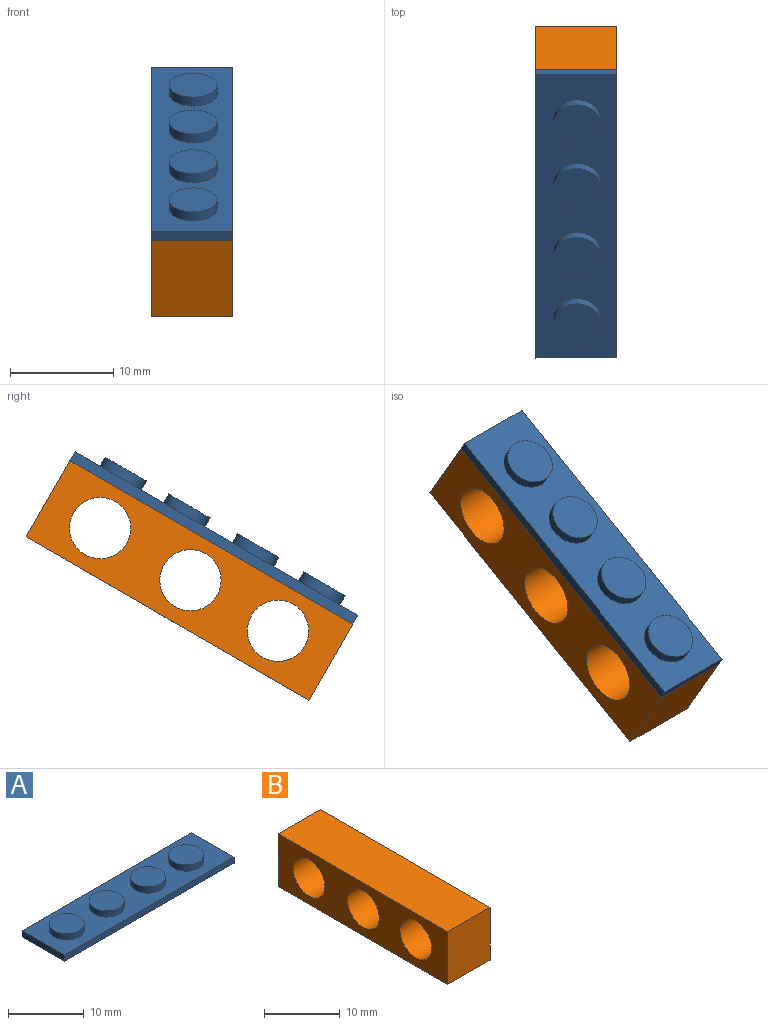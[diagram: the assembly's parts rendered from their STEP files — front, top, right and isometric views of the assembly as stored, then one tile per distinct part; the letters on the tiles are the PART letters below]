
ASSEMBLY  parts=2 mates=2
PART A: 14 faces, bbox 31.6x7.9x2 mm
  f0: cylinder r=2.31mm len=4.62mm, axis (0,0,-1), area 14.5mm2, adj f1,f12
  f1: plane 4.62x4.62mm, normal (0,0,1), area 16.8mm2, adj f0
  f2: cylinder r=2.31mm len=4.62mm, axis (0,0,-1), area 14.5mm2, adj f3,f12
  f3: plane 4.62x4.62mm, normal (0,0,1), area 16.8mm2, adj f2
  f4: cylinder r=2.31mm len=4.62mm, axis (0,0,-1), area 14.5mm2, adj f5,f12
  f5: plane 4.62x4.62mm, normal (0,0,1), area 16.8mm2, adj f4
  f6: cylinder r=2.31mm len=4.62mm, axis (0,0,-1), area 14.5mm2, adj f7,f12
  f7: plane 4.62x4.62mm, normal (0,0,1), area 16.8mm2, adj f6
  f8: plane 7.85x1mm, normal (-1,0,0), area 7.8mm2, adj f9,f11,f12,f13
  f9: plane 31.6x1mm, normal (0,-1,0), area 31.6mm2, adj f8,f10,f12,f13
  f10: plane 7.85x1mm, normal (1,0,0), area 7.8mm2, adj f9,f11,f12,f13
  f11: plane 31.6x1mm, normal (0,1,0), area 31.6mm2, adj f8,f10,f12,f13
  f12: plane 31.6x7.85mm, normal (0,0,1), area 181mm2, adj f0,f2,f4,f6,f8,f9,f10,f11
  f13: plane 31.6x7.85mm, normal (0,0,-1), area 248.1mm2, adj f8,f9,f10,f11
PART B: 20 faces, bbox 7.9x31.6x8.5 mm
  f0: plane 31.6x7.85mm, normal (0,0,-1), area 106mm2, adj f1,f2,f7,f8,f9,f10,f11,f15
  f1: plane 8.5x7.85mm, normal (0,-1,0), area 66.7mm2, adj f0,f6,f7,f8
  f2: plane 8.5x7.85mm, normal (0,1,0), area 66.7mm2, adj f0,f6,f7,f8
  f3: cylinder r=2.97mm len=7.85mm, axis (-1,0,0), area 146.3mm2, adj f7,f8
  f4: cylinder r=2.97mm len=7.85mm, axis (-1,0,0), area 146.3mm2, adj f7,f8
  f5: cylinder r=2.97mm len=7.85mm, axis (-1,0,0), area 146.3mm2, adj f7,f8
  f6: plane 31.6x7.85mm, normal (0,0,1), area 248.1mm2, adj f1,f2,f7,f8
  f7: plane 31.6x8.5mm, normal (1,0,0), area 185.7mm2, adj f0,f1,f2,f3,f4,f5,f6
  f8: plane 31.6x8.5mm, normal (-1,0,0), area 185.7mm2, adj f0,f1,f2,f3,f4,f5,f6
  f9: plane 4.95x1mm, normal (0,-1,0), area 5mm2, adj f0,f10,f15,f16
  f10: plane 28.7x1mm, normal (-1,0,0), area 28.7mm2, adj f0,f9,f11,f16
  f11: plane 4.95x1mm, normal (0,1,0), area 5mm2, adj f0,f10,f15,f16
  f12: cylinder r=1.53mm len=3.05mm, axis (0,0,-1), area 9.6mm2, adj f16,f17
  f13: cylinder r=1.53mm len=3.05mm, axis (0,0,-1), area 9.6mm2, adj f16,f18
  f14: cylinder r=1.53mm len=3.05mm, axis (0,0,-1), area 9.6mm2, adj f16,f19
  f15: plane 28.7x1mm, normal (1,0,0), area 28.7mm2, adj f0,f9,f11,f16
  f16: plane 28.7x4.95mm, normal (0,0,-1), area 120.1mm2, adj f9,f10,f11,f12,f13,f14,f15
  f17: plane 3.05x3.05mm, normal (0,0,-1), area 7.3mm2, adj f12
  f18: plane 3.05x3.05mm, normal (0,0,-1), area 7.3mm2, adj f13
  f19: plane 3.05x3.05mm, normal (0,0,-1), area 7.3mm2, adj f14
PLACE A rot(axis=(0.25,-0.25,0.94),93.8deg) t=(2.65,3.86,8.61)mm
PLACE B rot(axis=(1,0,0),30deg) t=(4.23,14.3,16.93)mm
MATE fastened A.f13 <-> A.f12  axis (0,0.5,-0.87) through (8.15,6.61,10.2)mm
MATE fastened A.f13 <-> B.f6  axis (0,0.5,-0.87) through (8.15,6.61,10.2)mm
